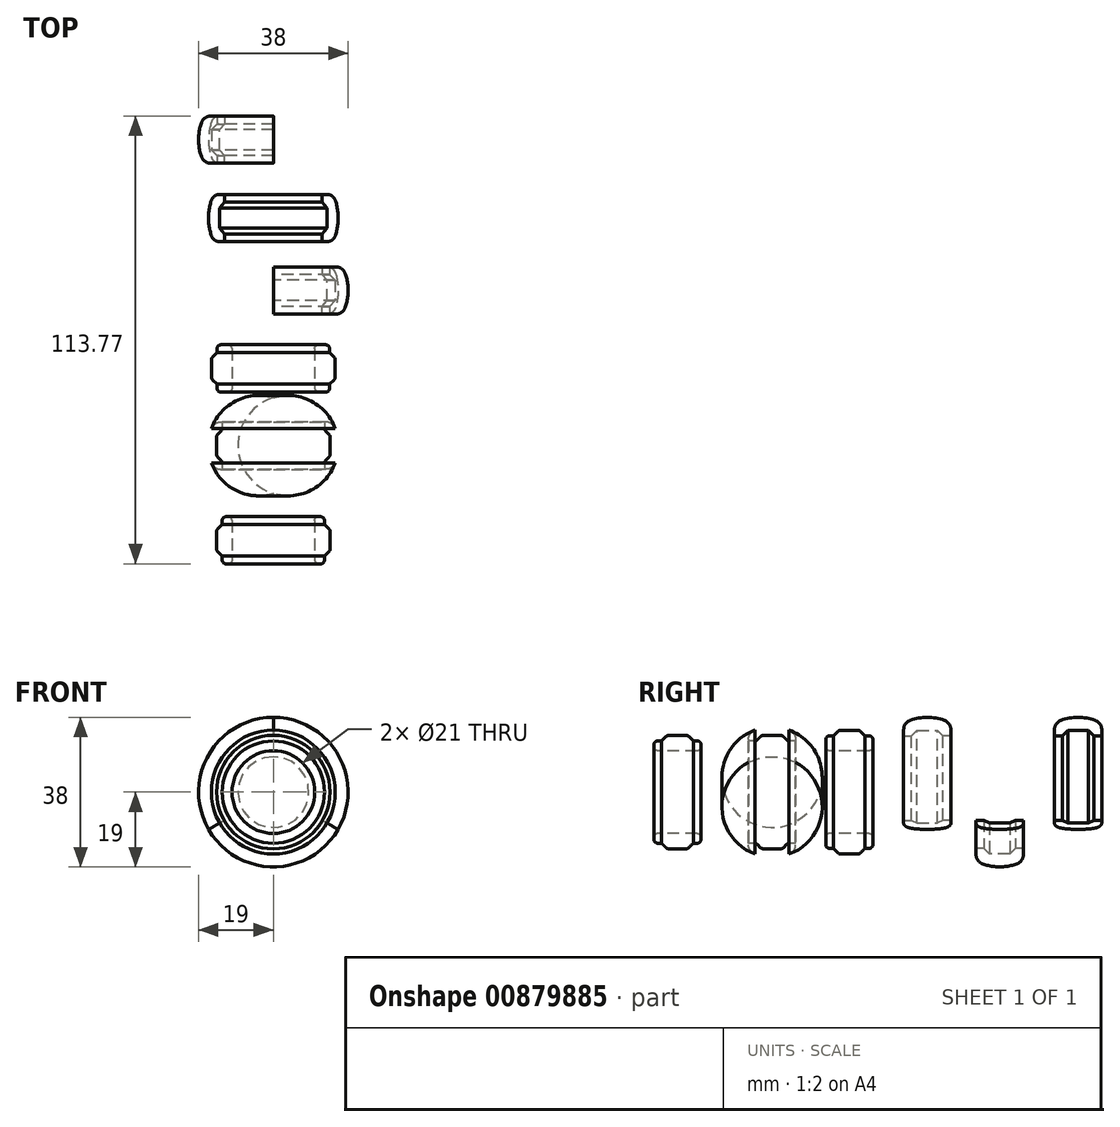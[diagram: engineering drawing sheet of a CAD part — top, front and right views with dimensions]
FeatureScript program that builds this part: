
annotation { "Feature Type Name" : "Feature", "Feature Type Description" : "" }
export const myFeature = defineFeature(function(context is Context, id is Id, definition is map)
    precondition{}
    {
        {
            var Q0;
            Q0=qCreatedBy(makeId("Right.planeOp"),FACE);
            var sketch = newSketch(context, id + "F0", { "sketchPlane" : qUnion([Q0])});
            skLineSegment(sketch, "E0.top", {"start": v(0, -7) * mm, "end": v(12, -7) * mm});
            skLineSegment(sketch, "E0.left", {"start": v(0, 0) * mm, "end": v(0, -7) * mm});
            skLineSegment(sketch, "E0.right", {"start": v(12, 0) * mm, "end": v(12, -7) * mm});
            skLineSegment(sketch, "E1", {"start": v(-0.03, -3.2) * mm, "end": v(1.97, -3.2) * mm});
            skLineSegment(sketch, "E2", {"start": v(12, -3.2) * mm, "end": v(10, -3.2) * mm});
            skLineSegment(sketch, "E3", {"start": v(1.97, -3.2) * mm, "end": v(3.38, -1.79) * mm});
            skLineSegment(sketch, "E4", {"start": v(10, -3.2) * mm, "end": v(8.59, -1.79) * mm});
            skLineSegment(sketch, "E5", {"start": v(3.38, -1.79) * mm, "end": v(8.59, -1.79) * mm});
            skArc(sketch, "E6", {"start": v(12, 0) * mm, "mid": v(6, 1.5) * mm, "end": v(0, 0) * mm});
            skPoint(sketch, "E7", {"position": v(6, 1.5) * mm});
            skPoint(sketch, "E8", {"position": v(6, 0) * mm});
            skLineSegment(sketch, "E9", {"start": v(-19.63, -17.5) * mm, "end": v(80.37, -17.5) * mm, "construction": true});
            skLineSegment(sketch, "E10.top", {"start": v(19.8, -7) * mm, "end": v(31.8, -7) * mm});
            skLineSegment(sketch, "E10.left", {"start": v(19.8, 0) * mm, "end": v(19.8, -7) * mm});
            skLineSegment(sketch, "E10.right", {"start": v(31.8, 0) * mm, "end": v(31.8, -7) * mm});
            skLineSegment(sketch, "E11", {"start": v(19.78, -3.2) * mm, "end": v(21.78, -3.2) * mm});
            skLineSegment(sketch, "E12", {"start": v(31.8, -3.2) * mm, "end": v(29.8, -3.2) * mm});
            skLineSegment(sketch, "E13", {"start": v(21.78, -3.2) * mm, "end": v(23.19, -1.79) * mm});
            skLineSegment(sketch, "E14", {"start": v(29.8, -3.2) * mm, "end": v(28.4, -1.79) * mm});
            skLineSegment(sketch, "E15", {"start": v(23.19, -1.79) * mm, "end": v(28.4, -1.79) * mm});
            skArc(sketch, "E16", {"start": v(31.8, 0) * mm, "mid": v(25.8, 1.5) * mm, "end": v(19.8, 0) * mm});
            skPoint(sketch, "E17", {"position": v(25.8, 1.5) * mm});
            skPoint(sketch, "E18", {"position": v(25.8, 0) * mm});
            skLineSegment(sketch, "E19.top", {"start": v(-19.63, -7) * mm, "end": v(-7.63, -7) * mm});
            skLineSegment(sketch, "E19.left", {"start": v(-19.63, -2.5) * mm, "end": v(-19.63, -7) * mm});
            skLineSegment(sketch, "E19.right", {"start": v(-7.63, -2.5) * mm, "end": v(-7.63, -7) * mm});
            skLineSegment(sketch, "E20", {"start": v(-19.66, -4.5) * mm, "end": v(-17.66, -4.5) * mm});
            skLineSegment(sketch, "E21", {"start": v(-7.63, -4.5) * mm, "end": v(-9.63, -4.5) * mm});
            skLineSegment(sketch, "E22", {"start": v(-17.66, -4.5) * mm, "end": v(-16.24, -3.09) * mm});
            skLineSegment(sketch, "E23", {"start": v(-9.63, -4.5) * mm, "end": v(-11.04, -3.09) * mm});
            skLineSegment(sketch, "E24", {"start": v(-16.24, -3.09) * mm, "end": v(-11.04, -3.09) * mm});
            skArc(sketch, "E25", {"start": v(-7.63, -2.5) * mm, "mid": v(-13.63, -1) * mm, "end": v(-19.63, -2.5) * mm});
            skPoint(sketch, "E26", {"position": v(-13.63, -1) * mm});
            skPoint(sketch, "E27", {"position": v(-13.63, -2.5) * mm});
            skLineSegment(sketch, "E28.top", {"start": v(38.2, -7) * mm, "end": v(50.2, -7) * mm});
            skLineSegment(sketch, "E28.left", {"start": v(38.2, 0) * mm, "end": v(38.2, -7) * mm});
            skLineSegment(sketch, "E28.right", {"start": v(50.2, 0) * mm, "end": v(50.2, -7) * mm});
            skLineSegment(sketch, "E29", {"start": v(38.18, -3.2) * mm, "end": v(40.18, -3.2) * mm});
            skLineSegment(sketch, "E30", {"start": v(50.2, -3.2) * mm, "end": v(48.2, -3.2) * mm});
            skLineSegment(sketch, "E31", {"start": v(40.18, -3.2) * mm, "end": v(41.6, -1.79) * mm});
            skLineSegment(sketch, "E32", {"start": v(48.2, -3.2) * mm, "end": v(46.8, -1.79) * mm});
            skLineSegment(sketch, "E33", {"start": v(41.6, -1.79) * mm, "end": v(46.8, -1.79) * mm});
            skArc(sketch, "E34", {"start": v(50.2, 0) * mm, "mid": v(44.2, 1.5) * mm, "end": v(38.2, 0) * mm});
            skPoint(sketch, "E35", {"position": v(44.2, 1.5) * mm});
            skPoint(sketch, "E36", {"position": v(44.2, 0) * mm});
            skLineSegment(sketch, "E37.top", {"start": v(58.12, -7) * mm, "end": v(70.12, -7) * mm});
            skLineSegment(sketch, "E37.left", {"start": v(58.12, 0) * mm, "end": v(58.12, -7) * mm});
            skLineSegment(sketch, "E37.right", {"start": v(70.12, 0) * mm, "end": v(70.12, -7) * mm});
            skLineSegment(sketch, "E38", {"start": v(58.1, -3.2) * mm, "end": v(60.1, -3.2) * mm});
            skLineSegment(sketch, "E39", {"start": v(70.12, -3.2) * mm, "end": v(68.12, -3.2) * mm});
            skLineSegment(sketch, "E40", {"start": v(60.1, -3.2) * mm, "end": v(61.5, -1.79) * mm});
            skLineSegment(sketch, "E41", {"start": v(68.12, -3.2) * mm, "end": v(66.7, -1.79) * mm});
            skLineSegment(sketch, "E42", {"start": v(61.5, -1.79) * mm, "end": v(66.7, -1.79) * mm});
            skArc(sketch, "E43", {"start": v(70.12, 0) * mm, "mid": v(64.12, 1.5) * mm, "end": v(58.12, 0) * mm});
            skPoint(sketch, "E44", {"position": v(64.12, 1.5) * mm});
            skPoint(sketch, "E45", {"position": v(64.12, 0) * mm});
            skLineSegment(sketch, "E46", {"start": v(-43.65, -17.5) * mm, "end": v(56.35, -17.5) * mm, "construction": true});
            skLineSegment(sketch, "E47.top", {"start": v(-43.65, -7) * mm, "end": v(-31.65, -7) * mm});
            skLineSegment(sketch, "E47.left", {"start": v(-43.65, -2.5) * mm, "end": v(-43.65, -7) * mm});
            skLineSegment(sketch, "E47.right", {"start": v(-31.65, -2.5) * mm, "end": v(-31.65, -7) * mm});
            skLineSegment(sketch, "E48", {"start": v(-43.68, -4.5) * mm, "end": v(-41.68, -4.5) * mm});
            skLineSegment(sketch, "E49", {"start": v(-31.65, -4.5) * mm, "end": v(-33.65, -4.5) * mm});
            skLineSegment(sketch, "E50", {"start": v(-41.68, -4.5) * mm, "end": v(-40.27, -3.09) * mm});
            skLineSegment(sketch, "E51", {"start": v(-33.65, -4.5) * mm, "end": v(-35.07, -3.09) * mm});
            skLineSegment(sketch, "E52", {"start": v(-40.27, -3.09) * mm, "end": v(-35.07, -3.09) * mm});
            skArc(sketch, "E53", {"start": v(-31.65, -2.5) * mm, "mid": v(-37.65, -1) * mm, "end": v(-43.65, -2.5) * mm});
            skPoint(sketch, "E54", {"position": v(-37.65, -1) * mm});
            skPoint(sketch, "E55", {"position": v(-37.65, -2.5) * mm});
            skSolve(sketch);
        }
        {
            var Q0;
            {var subQ1=sQuery(id+"F0.wireOp",EDGE,"E0.top");Q0=makeQuery(id+"F0.imprint","IMPRINT",FACE,{"disambiguationData":[TD([[makeQuery(id+"F0.imprint","IMPRINT",EDGE,{"derivedFrom":subQ1}),1.0]])]});}
            var Q1;
            Q1=sQuery(id+"F0.wireOp",EDGE,"E9");
            revolve(context, id + "F1", {"surfaceOperationType" : NewSurfaceOperationType.NEW, "entities" : qUnion([Q0]), "axis" : qUnion([Q1]), "revolveType" : RevolveType.FULL});
        }
        {
            var Q0;
            Q0=makeQuery(id+"F1.opRevolve","SWEPT_EDGE",EDGE,{"disambiguationData":[OSD([sQuery(id+"F0.wireOp",EDGE,"E3"),sQuery(id+"F0.wireOp",EDGE,"E5")])]});
            var Q1;
            Q1=makeQuery(id+"F1.opRevolve","SWEPT_EDGE",EDGE,{"disambiguationData":[OSD([sQuery(id+"F0.wireOp",EDGE,"E0.left"),sQuery(id+"F0.wireOp",EDGE,"E1")])]});
            var Q2;
            Q2=makeQuery(id+"F1.opRevolve","SWEPT_EDGE",EDGE,{"disambiguationData":[OSD([sQuery(id+"F0.wireOp",EDGE,"E4"),sQuery(id+"F0.wireOp",EDGE,"E5")])]});
            var Q3;
            Q3=makeQuery(id+"F1.opRevolve","SWEPT_EDGE",EDGE,{"disambiguationData":[OSD([sQuery(id+"F0.wireOp",EDGE,"E0.right"),sQuery(id+"F0.wireOp",EDGE,"E2")])]});
            fillet(context, id + "F2", {"entities" : qUnion([Q0, Q1, Q2, Q3]), "radius" : 1 * mm, "tangentPropagation" : true, "allowEdgeOverflow" : false});
        }
        {
            var Q0;
            {var subQ6=sQuery(id+"F0.wireOp",EDGE,"E21");Q0=makeQuery(id+"F0.imprint","IMPRINT",FACE,{"disambiguationData":[TD([[makeQuery(id+"F0.imprint","IMPRINT",EDGE,{"derivedFrom":subQ6}),-1.0]])]});}
            var Q1;
            Q1=sQuery(id+"F0.wireOp",EDGE,"E9");
            revolve(context, id + "F3", {"surfaceOperationType" : NewSurfaceOperationType.NEW, "entities" : qUnion([Q0]), "axis" : qUnion([Q1]), "revolveType" : RevolveType.FULL});
        }
        {
            var Q0;
            Q0=makeQuery(id+"F3.opRevolve","SWEPT_EDGE",EDGE,{"disambiguationData":[OSD([sQuery(id+"F0.wireOp",EDGE,"E20"),sQuery(id+"F0.wireOp",EDGE,"E22")])]});
            var Q1;
            Q1=makeQuery(id+"F3.opRevolve","SWEPT_EDGE",EDGE,{"disambiguationData":[OSD([sQuery(id+"F0.wireOp",EDGE,"E22"),sQuery(id+"F0.wireOp",EDGE,"E24")])]});
            var Q2;
            Q2=makeQuery(id+"F3.opRevolve","SWEPT_EDGE",EDGE,{"disambiguationData":[OSD([sQuery(id+"F0.wireOp",EDGE,"E21"),sQuery(id+"F0.wireOp",EDGE,"E23")])]});
            var Q3;
            Q3=makeQuery(id+"F3.opRevolve","SWEPT_EDGE",EDGE,{"disambiguationData":[OSD([sQuery(id+"F0.wireOp",EDGE,"E23"),sQuery(id+"F0.wireOp",EDGE,"E24")])]});
            fillet(context, id + "F4", {"entities" : qUnion([Q0, Q1, Q2, Q3]), "radius" : 1 * mm, "tangentPropagation" : true, "allowEdgeOverflow" : false});
        }
        {
            var Q0;
            Q0=makeQuery(id+"F3.opRevolve","SWEPT_EDGE",EDGE,{"disambiguationData":[OSD([sQuery(id+"F0.wireOp",EDGE,"E19.left"),sQuery(id+"F0.wireOp",EDGE,"E25")])]});
            var Q1;
            Q1=makeQuery(id+"F3.opRevolve","SWEPT_EDGE",EDGE,{"disambiguationData":[OSD([sQuery(id+"F0.wireOp",EDGE,"E19.right"),sQuery(id+"F0.wireOp",EDGE,"E25")])]});
            fillet(context, id + "F5", {"entities" : qUnion([Q0, Q1]), "radius" : 2.5 * mm, "tangentPropagation" : true, "allowEdgeOverflow" : false});
        }
        {
            var Q0;
            Q0=makeQuery(id+"F1.opRevolve","SWEPT_EDGE",EDGE,{"disambiguationData":[OSD([sQuery(id+"F0.wireOp",EDGE,"E0.top"),sQuery(id+"F0.wireOp",EDGE,"E0.right")])]});
            var Q1;
            Q1=makeQuery(id+"F1.opRevolve","SWEPT_EDGE",EDGE,{"disambiguationData":[OSD([sQuery(id+"F0.wireOp",EDGE,"E0.top"),sQuery(id+"F0.wireOp",EDGE,"E0.left")])]});
            fillet(context, id + "F6", {"entities" : qUnion([Q0, Q1]), "radius" : 1 * mm, "tangentPropagation" : true, "allowEdgeOverflow" : false});
        }
        {
            var Q0;
            {var subQ6=sQuery(id+"F0.wireOp",EDGE,"E12");Q0=makeQuery(id+"F0.imprint","IMPRINT",FACE,{"disambiguationData":[TD([[makeQuery(id+"F0.imprint","IMPRINT",EDGE,{"derivedFrom":subQ6}),-1.0]])]});}
            var Q1;
            Q1=sQuery(id+"F0.wireOp",EDGE,"E9");
            revolve(context, id + "F7", {"surfaceOperationType" : NewSurfaceOperationType.NEW, "entities" : qUnion([Q0]), "axis" : qUnion([Q1]), "revolveType" : RevolveType.ONE_DIRECTION, "angle" : 120 * degree});
        }
        {
            var Q0;
            {var subQ6=sQuery(id+"F0.wireOp",EDGE,"E30");Q0=makeQuery(id+"F0.imprint","IMPRINT",FACE,{"disambiguationData":[TD([[makeQuery(id+"F0.imprint","IMPRINT",EDGE,{"derivedFrom":subQ6}),-1.0]])]});}
            var Q1;
            Q1=sQuery(id+"F0.wireOp",EDGE,"E9");
            revolve(context, id + "F8", {"surfaceOperationType" : NewSurfaceOperationType.NEW, "entities" : qUnion([Q0]), "axis" : qUnion([Q1]), "revolveType" : RevolveType.TWO_DIRECTIONS, "angle" : 240 * degree, "angleBack" : 120 * degree});
        }
        {
            var Q0;
            {var subQ6=sQuery(id+"F0.wireOp",EDGE,"E39");Q0=makeQuery(id+"F0.imprint","IMPRINT",FACE,{"disambiguationData":[TD([[makeQuery(id+"F0.imprint","IMPRINT",EDGE,{"derivedFrom":subQ6}),-1.0]])]});}
            var Q1;
            Q1=sQuery(id+"F0.wireOp",EDGE,"E9");
            revolve(context, id + "F9", {"surfaceOperationType" : NewSurfaceOperationType.NEW, "entities" : qUnion([Q0]), "axis" : qUnion([Q1]), "revolveType" : RevolveType.TWO_DIRECTIONS, "angle" : 360 * degree, "angleBack" : 240 * degree});
        }
        {
            var Q0;
            Q0=makeQuery(id+"F7.opRevolve","SWEPT_EDGE",EDGE,{"disambiguationData":[OSD([sQuery(id+"F0.wireOp",EDGE,"E10.left"),sQuery(id+"F0.wireOp",EDGE,"E16")])]});
            var Q1;
            Q1=makeQuery(id+"F7.opRevolve","SWEPT_EDGE",EDGE,{"disambiguationData":[OSD([sQuery(id+"F0.wireOp",EDGE,"E10.right"),sQuery(id+"F0.wireOp",EDGE,"E16")])]});
            var Q2;
            Q2=makeQuery(id+"F8.opRevolve","SWEPT_EDGE",EDGE,{"disambiguationData":[OSD([sQuery(id+"F0.wireOp",EDGE,"E28.right"),sQuery(id+"F0.wireOp",EDGE,"E34")])]});
            var Q3;
            Q3=makeQuery(id+"F8.opRevolve","SWEPT_EDGE",EDGE,{"disambiguationData":[OSD([sQuery(id+"F0.wireOp",EDGE,"E28.left"),sQuery(id+"F0.wireOp",EDGE,"E34")])]});
            var Q4;
            Q4=makeQuery(id+"F9.opRevolve","SWEPT_EDGE",EDGE,{"disambiguationData":[OSD([sQuery(id+"F0.wireOp",EDGE,"E37.right"),sQuery(id+"F0.wireOp",EDGE,"E43")])]});
            var Q5;
            Q5=makeQuery(id+"F9.opRevolve","SWEPT_EDGE",EDGE,{"disambiguationData":[OSD([sQuery(id+"F0.wireOp",EDGE,"E37.left"),sQuery(id+"F0.wireOp",EDGE,"E43")])]});
            fillet(context, id + "F10", {"entities" : qUnion([Q0, Q1, Q2, Q3, Q4, Q5]), "radius" : 2.5 * mm, "tangentPropagation" : true, "allowEdgeOverflow" : false});
        }
        {
            var Q0;
            {var subQ1=sQuery(id+"F0.wireOp",EDGE,"E47.top");Q0=makeQuery(id+"F0.imprint","IMPRINT",FACE,{"disambiguationData":[TD([[makeQuery(id+"F0.imprint","IMPRINT",EDGE,{"derivedFrom":subQ1}),1.0]])]});}
            var Q1;
            Q1=sQuery(id+"F0.wireOp",EDGE,"E46");
            revolve(context, id + "F11", {"surfaceOperationType" : NewSurfaceOperationType.NEW, "entities" : qUnion([Q0]), "axis" : qUnion([Q1]), "revolveType" : RevolveType.FULL});
        }
        {
            var Q0;
            Q0=makeQuery(id+"F11.opRevolve","SWEPT_EDGE",EDGE,{"disambiguationData":[OSD([sQuery(id+"F0.wireOp",EDGE,"E50"),sQuery(id+"F0.wireOp",EDGE,"E52")])]});
            var Q1;
            Q1=makeQuery(id+"F11.opRevolve","SWEPT_EDGE",EDGE,{"disambiguationData":[OSD([sQuery(id+"F0.wireOp",EDGE,"E51"),sQuery(id+"F0.wireOp",EDGE,"E52")])]});
            var Q2;
            Q2=makeQuery(id+"F11.opRevolve","SWEPT_EDGE",EDGE,{"disambiguationData":[OSD([sQuery(id+"F0.wireOp",EDGE,"E47.left"),sQuery(id+"F0.wireOp",EDGE,"E48")])]});
            var Q3;
            Q3=makeQuery(id+"F11.opRevolve","SWEPT_EDGE",EDGE,{"disambiguationData":[OSD([sQuery(id+"F0.wireOp",EDGE,"E47.right"),sQuery(id+"F0.wireOp",EDGE,"E49")])]});
            var Q4;
            Q4=makeQuery(id+"F11.opRevolve","SWEPT_EDGE",EDGE,{"disambiguationData":[OSD([sQuery(id+"F0.wireOp",EDGE,"E47.top"),sQuery(id+"F0.wireOp",EDGE,"E47.left")])]});
            var Q5;
            Q5=makeQuery(id+"F11.opRevolve","SWEPT_EDGE",EDGE,{"disambiguationData":[OSD([sQuery(id+"F0.wireOp",EDGE,"E47.top"),sQuery(id+"F0.wireOp",EDGE,"E47.right")])]});
            fillet(context, id + "F12", {"entities" : qUnion([Q0, Q1, Q2, Q3, Q4, Q5]), "radius" : 1 * mm, "tangentPropagation" : true, "allowEdgeOverflow" : false});
        }
    });
